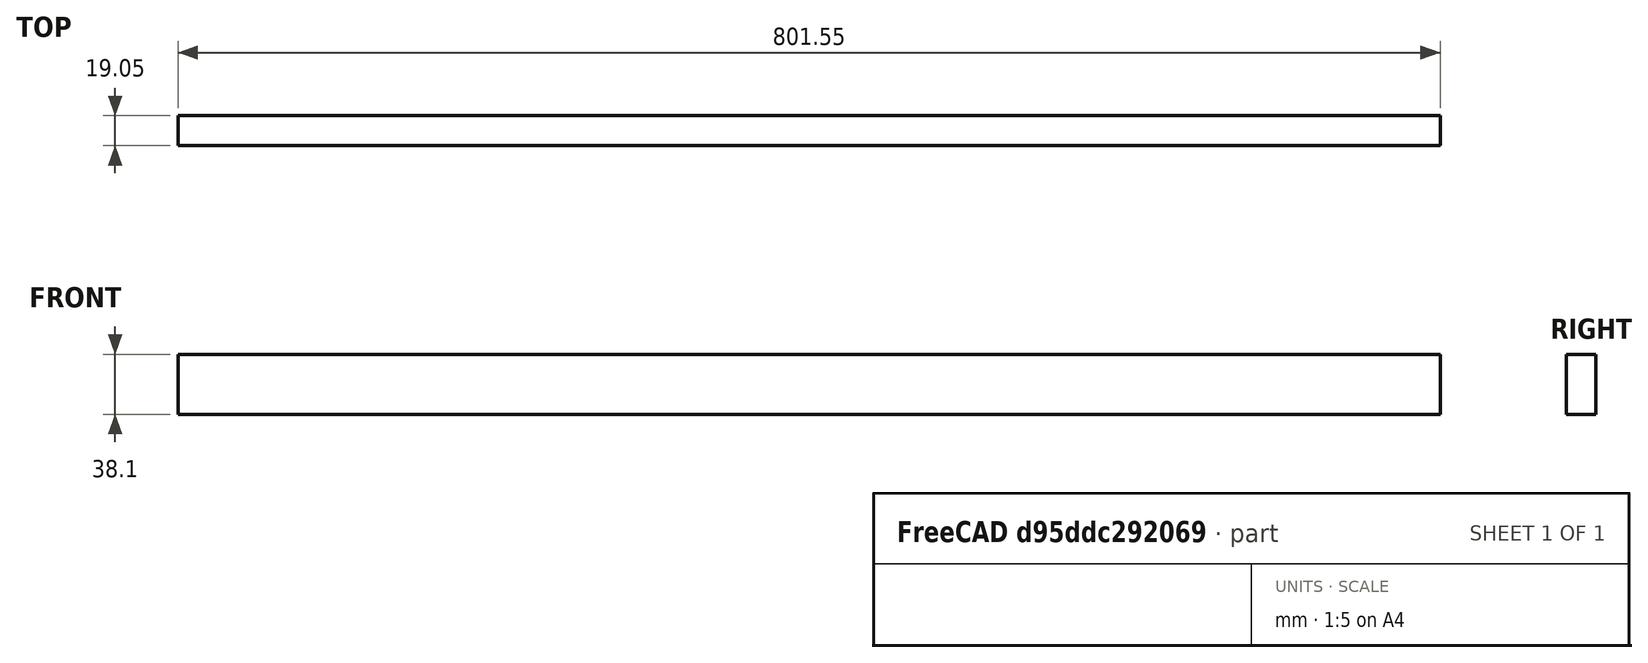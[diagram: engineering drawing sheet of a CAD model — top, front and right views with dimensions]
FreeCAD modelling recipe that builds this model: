
FCSTD DOCUMENT  (FreeCAD 0.20R29177 (Git))
Label: topRightFrontBand
License: All rights reserved
LicenseURL: http://en.wikipedia.org/wiki/All_rights_reserved
objects: Sketcher::SketchObject×1, PartDesign::Pad×1, PartDesign::Body×1
note: 4 computed .brp shape members not serialized (recipe doc carries the construction recipe); baked Part::Feature solids carry a one-line shape summary decoded from their .brp

FEATURE [Sketcher::SketchObject] Sketch
  FullyConstrained = true
  MapMode = 5
  Placement = pos=(0,0,0) rot=(1,0,0;1.5708rad)
  Support = -> [XZ_Plane001]
  expr: Constraints[10] = 1.5 * 25.4
  expr: Constraints[9] = 801.55
  sketch-geometry (4):
    g0: LineSegment StartX=0 StartY=0 StartZ=0 EndX=801.55 EndY=0 EndZ=0
    g1: LineSegment StartX=801.55 StartY=0 StartZ=0 EndX=801.55 EndY=38.1 EndZ=0
    g2: LineSegment StartX=801.55 StartY=38.1 StartZ=0 EndX=0 EndY=38.1 EndZ=0
    g3: LineSegment StartX=0 StartY=38.1 StartZ=0 EndX=0 EndY=0 EndZ=0
  constraints (11):
    c: Coincident(g0,g1)
    c: Coincident(g1,g2)
    c: Coincident(g2,g3)
    c: Coincident(g3,g0)
    c: Horizontal(g0)
    c: Horizontal(g2)
    c: Vertical(g1)
    c: Vertical(g3)
    c: Coincident(g0,g-1)
    c: DistanceX(g0,g0) = 801.55
    c: DistanceY(g3,g3) = 38.1
FEATURE [PartDesign::Pad] Pad
  Direction = (0,-1,-2e-16)
  Length = 19.05
  Length2 = 10
  Placement = pos=(0,0,0) rot=(1,0,0;1.5708rad)
  Profile = -> Sketch
  ReferenceAxis = -> Sketch [N_Axis]
  Type = 0
  expr: Length = 3 / 4 * 25.4
FEATURE [PartDesign::Body] Body001
  Group = -> [Sketch,Pad]
  Origin = -> Origin001
  Tip = -> Pad
